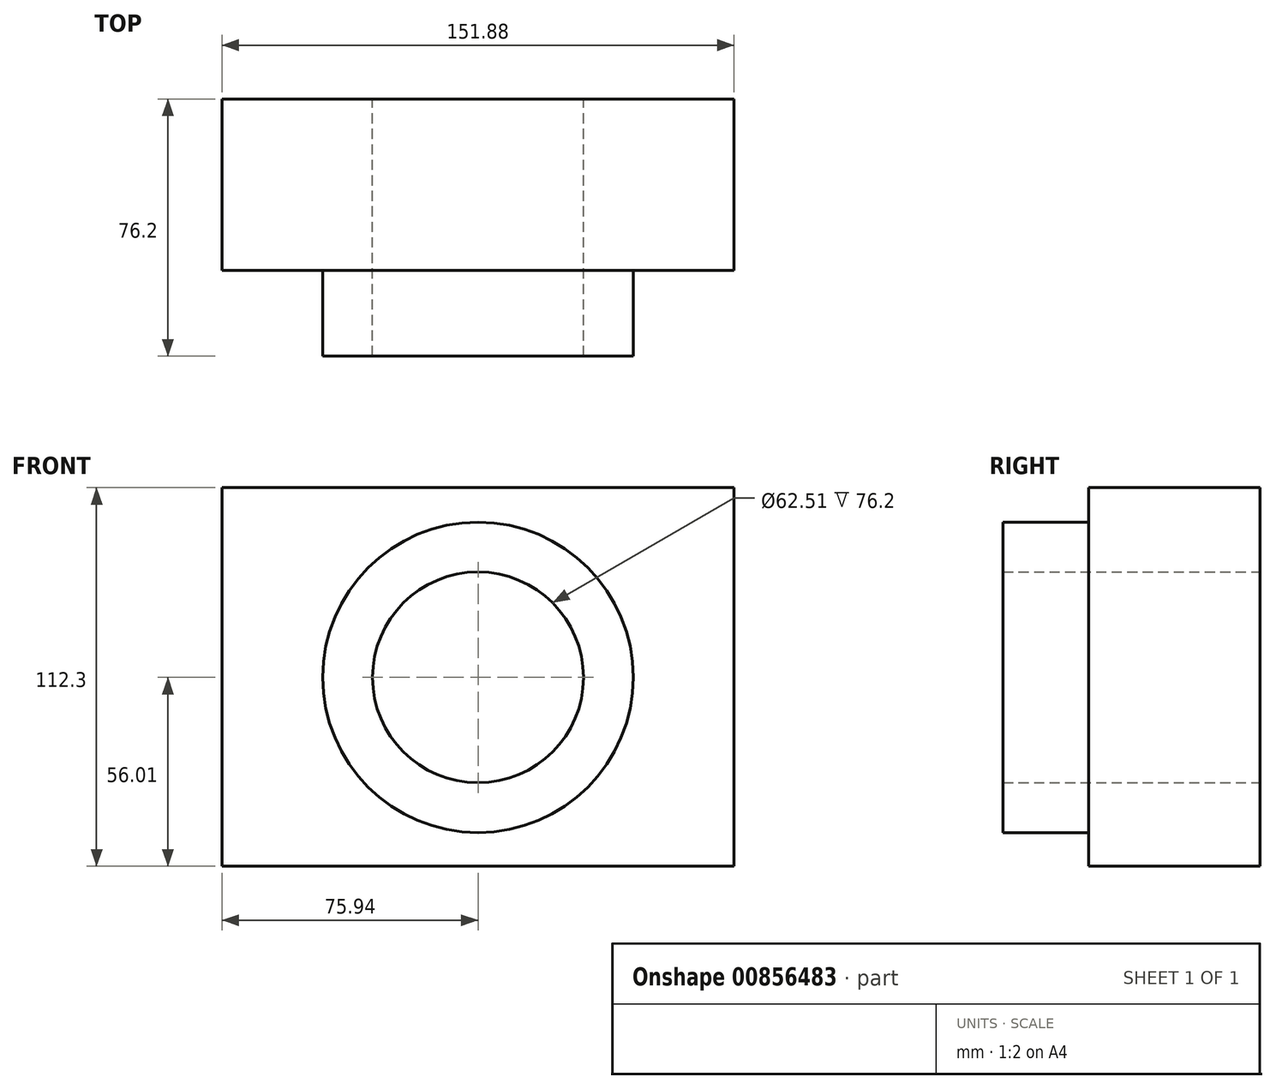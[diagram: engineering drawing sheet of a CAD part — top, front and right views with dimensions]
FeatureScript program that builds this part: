
annotation { "Feature Type Name" : "Feature", "Feature Type Description" : "" }
export const myFeature = defineFeature(function(context is Context, id is Id, definition is map)
    precondition{}
    {
        {
            var Q0;
            Q0=qCreatedBy(makeId("Front.planeOp"),FACE);
            var sketch = newSketch(context, id + "F0", { "sketchPlane" : qUnion([Q0])});
            skLineSegment(sketch, "E0.bottom", {"start": v(-56.57, 59.66) * mm, "end": v(58.25, 59.66) * mm});
            skLineSegment(sketch, "E0.top", {"start": v(-56.57, -55.16) * mm, "end": v(58.25, -55.16) * mm});
            skLineSegment(sketch, "E0.left", {"start": v(-56.57, 59.66) * mm, "end": v(-56.57, -55.16) * mm});
            skLineSegment(sketch, "E0.right", {"start": v(58.25, 59.66) * mm, "end": v(58.25, -55.16) * mm});
            skCircle(sketch, "E1", {"center": v(0, 0) * mm, "radius": 46.03 * mm});
            skCircle(sketch, "E2", {"center": v(0, 0) * mm, "radius": 31.26 * mm});
            skSolve(sketch);
        }
        {
            var Q0;
            Q0=makeQuery(id+"F0.imprint","IMPRINT",FACE,{"disambiguationData":[TD([[makeQuery(id+"F0.imprint","IMPRINT",EDGE,{"derivedFrom":sQuery(id+"F0.wireOp",EDGE,"E1")}),1.0]])]});
            extrude(context, id + "F1", {"entities" : qUnion([Q0]), "depth" : 25.4 * mm, "offsetDistance" : 25.4 * mm});
        }
        {
            var Q0;
            Q0=qCreatedBy(makeId("Front.planeOp"),FACE);
            var sketch = newSketch(context, id + "F2", { "sketchPlane" : qUnion([Q0])});
            skLineSegment(sketch, "E3.bottom", {"start": v(-75.94, 56.29) * mm, "end": v(75.94, 56.29) * mm});
            skLineSegment(sketch, "E3.top", {"start": v(-75.94, -56) * mm, "end": v(75.94, -56) * mm});
            skLineSegment(sketch, "E3.left", {"start": v(-75.94, 56.29) * mm, "end": v(-75.94, -56) * mm});
            skLineSegment(sketch, "E3.right", {"start": v(75.94, 56.29) * mm, "end": v(75.94, -56) * mm});
            skSolve(sketch);
        }
        {
            var Q0;
            Q0 = qSketchRegion(id + "F2", true);
            extrude(context, id + "F3", {"entities" : qUnion([Q0]), "operationType" : NewBodyOperationType.ADD, "oppositeDirection" : true, "depth" : 50.8 * mm, "offsetDistance" : 25.4 * mm});
        }
        {
            var Q0;
            Q0=makeQuery(id+"F3.boolean.opBoolean","SPLIT",FACE,{"disambiguationData":[TD([makeQuery(id+"F1.opExtrude","SWEPT_FACE",FACE,{"disambiguationData":[OSD([sQuery(id+"F0.wireOp",EDGE,"E2")])]})])],"derivedFrom":makeQuery(id+"F3.opExtrude","CAP_FACE",FACE,{"disambiguationData":[OSD([sQuery(id+"F2.wireOp",EDGE,"E3.bottom"),sQuery(id+"F2.wireOp",EDGE,"E3.top"),sQuery(id+"F2.wireOp",EDGE,"E3.left"),sQuery(id+"F2.wireOp",EDGE,"E3.right")])],"isStart":true})});
            extrude(context, id + "F4", {"entities" : qUnion([Q0]), "operationType" : NewBodyOperationType.REMOVE, "oppositeDirection" : true, "depth" : 134.37 * mm, "offsetDistance" : 25.4 * mm});
        }
    });
